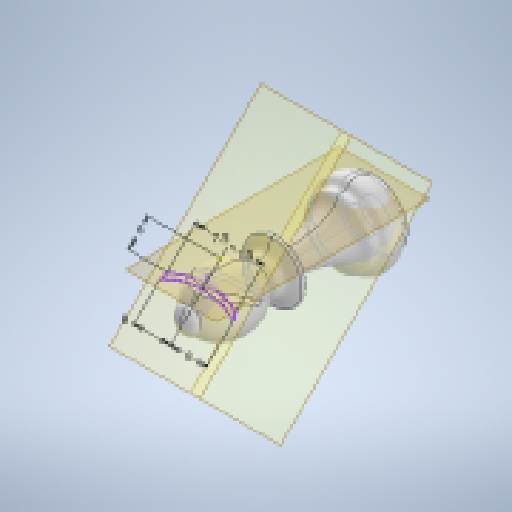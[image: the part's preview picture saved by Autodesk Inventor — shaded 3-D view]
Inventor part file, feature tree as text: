
AUTODESK INVENTOR PART (.ipt)
format: ipt  version: 2024.1 (Build 281209000, 209)  size: 447,488 bytes
history: native  units: mm
features: sketch x5, plane x3, extrude x2, other x1, revolve x1, fillet x1, sweep x1, projected_geometry x1
ambient origin geometry x8: Origin, YZ Plane, XZ Plane, XY Plane, X Axis, Y Axis, Z Axis, Center Point
bodies: Solid1 (feature_tree)
feature tree (15):
  extrude  "Extrusion1"  Depth=3.0mm TaperAngle=0.0deg
  other  "Work Axis1"
  extrude  "Extrusion2"  Depth=14.3mm
  revolve  "Revolution1"  [1 undecoded]
  fillet  "Fillet5"  Radius=0.6mm
  plane  "Work Plane6"
  plane  "Work Plane9"
  sweep  "Sweep1"
  sketch  "Sketch1"  dims[d0=10.0mm d1=3.0mm d2=0.0mm]
  sketch  "Sketch2"  dims[d5=360.0deg d6=14.3mm]
  sketch  "Sketch3"  dims[d7=3.0mm d8=0.0mm d89=12.3mm d107=0.6mm]
  projected_geometry  "Projected Loop1"
  plane  "Work Plane7"
  sketch  "Sketch16"  dims[d127=2.8mm d128=1.4mm]
  sketch  "Sketch17"  dims[d129=6.5mm d130=8.0mm d131=8.0mm d132=33.0mm d133=11.2mm d134=6.75mm d135=0.8mm d136=25.0mm d137=8.0mm d138=8.0mm d141=6.0mm d142=7.5mm d143=7.5mm d144=0.0mm d145=0.0mm d98=0.0mm d99=0.0mm d100=0.0mm d101=0.0mm]
note: 1 required parameter value undecoded (feature->parameter linkage not recoverable at this tier; creation-order binding heuristic only, values carry confidence <= 0.55)
